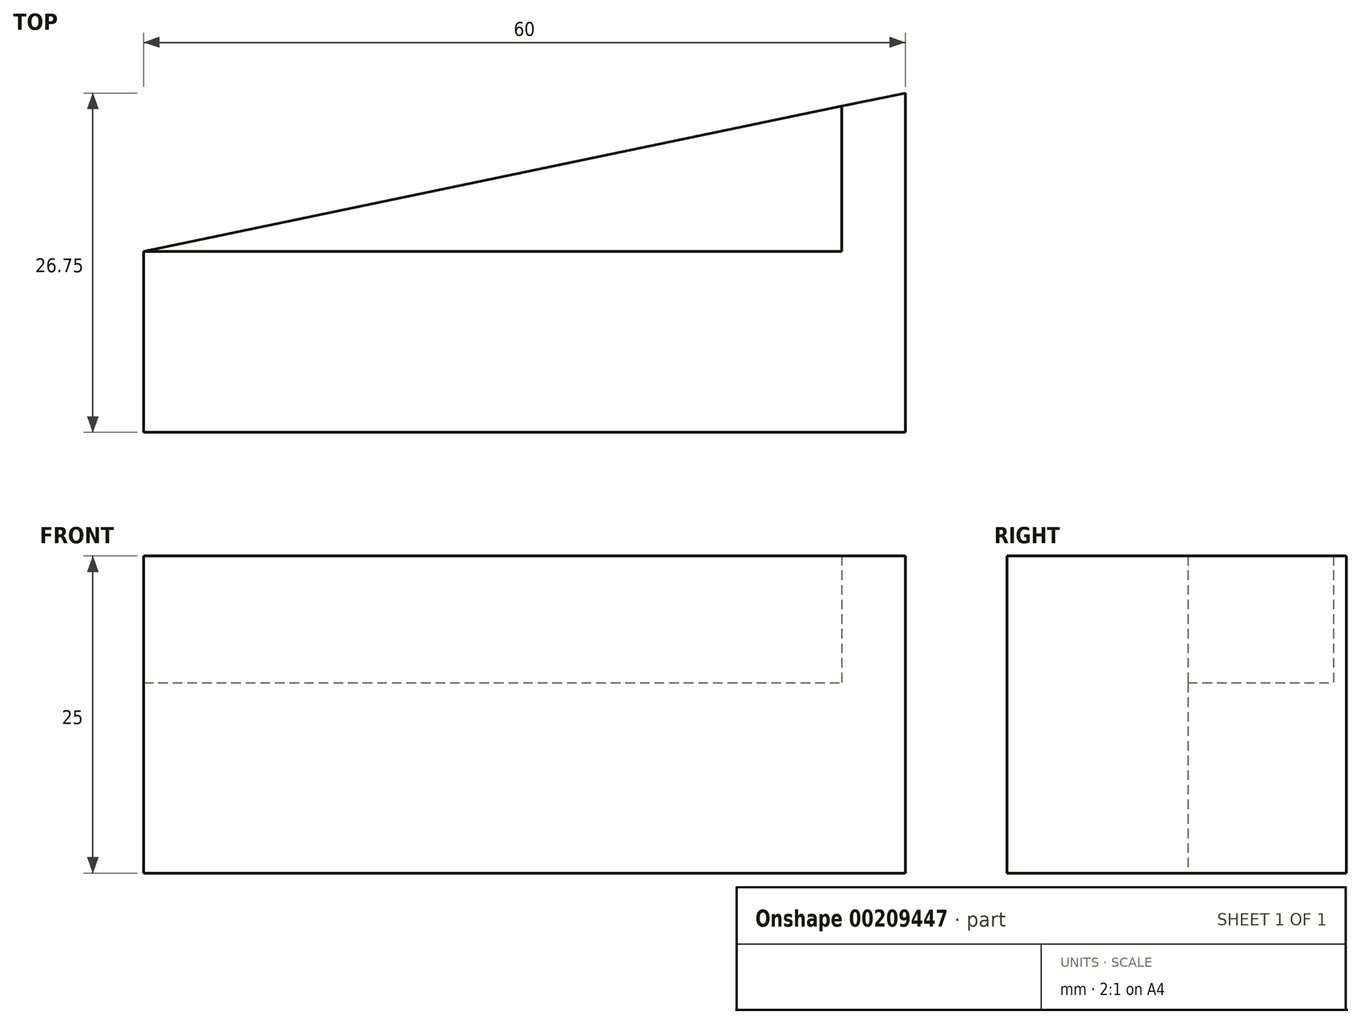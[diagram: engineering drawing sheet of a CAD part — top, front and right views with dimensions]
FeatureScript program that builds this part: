
annotation { "Feature Type Name" : "Feature", "Feature Type Description" : "" }
export const myFeature = defineFeature(function(context is Context, id is Id, definition is map)
    precondition{}
    {
        {
            var Q0;
            Q0=qCreatedBy(makeId("Top.planeOp"),FACE);
            var sketch = newSketch(context, id + "F0", { "sketchPlane" : qUnion([Q0])});
            skLineSegment(sketch, "E0", {"start": v(30, 0) * mm, "end": v(60, 0) * mm});
            skLineSegment(sketch, "E1", {"start": v(60, 0) * mm, "end": v(90, 0) * mm});
            skLineSegment(sketch, "E2", {"start": v(90, 0) * mm, "end": v(90, 18.75) * mm});
            skLineSegment(sketch, "E3", {"start": v(60, 0) * mm, "end": v(60, 12.5) * mm});
            skLineSegment(sketch, "E4", {"start": v(30, 6.25) * mm, "end": v(90, 18.75) * mm});
            skLineSegment(sketch, "E5", {"start": v(30, 0) * mm, "end": v(30, 6.25) * mm});
            skSolve(sketch);
        }
        {
            var Q0;
            Q0=qSketchRegion(id+"F0",true);
            extrude(context, id + "F1", {"entities" : qUnion([Q0]), "depth" : 15 * mm});
        }
        {
            var Q0;
            Q0=makeQuery(id+"F1.opExtrude","CAP_FACE",FACE,{"disambiguationData":[OSD([sQuery(id+"F0.wireOp",EDGE,"E0"),sQuery(id+"F0.wireOp",EDGE,"HZKhCLW9-oDJk-jZ79-Cc5a-FlSk4M4CYGuW"),sQuery(id+"F0.wireOp",EDGE,"E1"),sQuery(id+"F0.wireOp",EDGE,"E2")])],"isStart":false});
            var sketch = newSketch(context, id + "F2", { "sketchPlane" : qUnion([Q0])});
            skLineSegment(sketch, "E6", {"start": v(90, 0) * mm, "end": v(90, 0) * mm});
            skLineSegment(sketch, "E7", {"start": v(90, 0) * mm, "end": v(30, 0) * mm});
            skLineSegment(sketch, "E8", {"start": v(90, 0) * mm, "end": v(90, 18.75) * mm});
            skLineSegment(sketch, "E9.0", {"start": v(85, 6.25) * mm, "end": v(85, 17.7) * mm});
            skLineSegment(sketch, "E10", {"start": v(30, 6.25) * mm, "end": v(85, 6.25) * mm});
            skLineSegment(sketch, "E11", {"start": v(30, 6.25) * mm, "end": v(30, 0) * mm});
            skLineSegment(sketch, "E12", {"start": v(90, 18.75) * mm, "end": v(85, 17.7) * mm});
            skSolve(sketch);
        }
        {
            var Q0;
            Q0=qSketchRegion(id+"F2",true);
            extrude(context, id + "F3", {"entities" : qUnion([Q0]), "operationType" : NewBodyOperationType.ADD, "depth" : 10 * mm});
        }
        {
            var Q0;
            Q0=makeQuery(id+"F3.boolean.opBoolean","MERGE",FACE,{"derivedFrom":[makeQuery(id+"F1.opExtrude","SWEPT_FACE",FACE,{"disambiguationData":[OSD([sQuery(id+"F0.wireOp",EDGE,"E0"),sQuery(id+"F0.wireOp",EDGE,"E1")])]}),makeQuery(id+"F3.opExtrude","SWEPT_FACE",FACE,{"disambiguationData":[OSD([sQuery(id+"F2.wireOp",EDGE,"E7")])]})]});
            extrude(context, id + "F4", {"entities" : qUnion([Q0]), "operationType" : NewBodyOperationType.ADD, "depth" : 3 * mm});
        }
        {
            var Q0;
            Q0=makeQuery(id+"F4.opExtrude","CAP_FACE",FACE,{"disambiguationData":[OSD([sQuery(id+"F0.wireOp",EDGE,"E0"),sQuery(id+"F0.wireOp",EDGE,"E1"),sQuery(id+"F2.wireOp",EDGE,"E7")])],"isStart":false});
            extrude(context, id + "F5", {"entities" : qUnion([Q0]), "operationType" : NewBodyOperationType.ADD, "depth" : 5 * mm});
        }
    });
